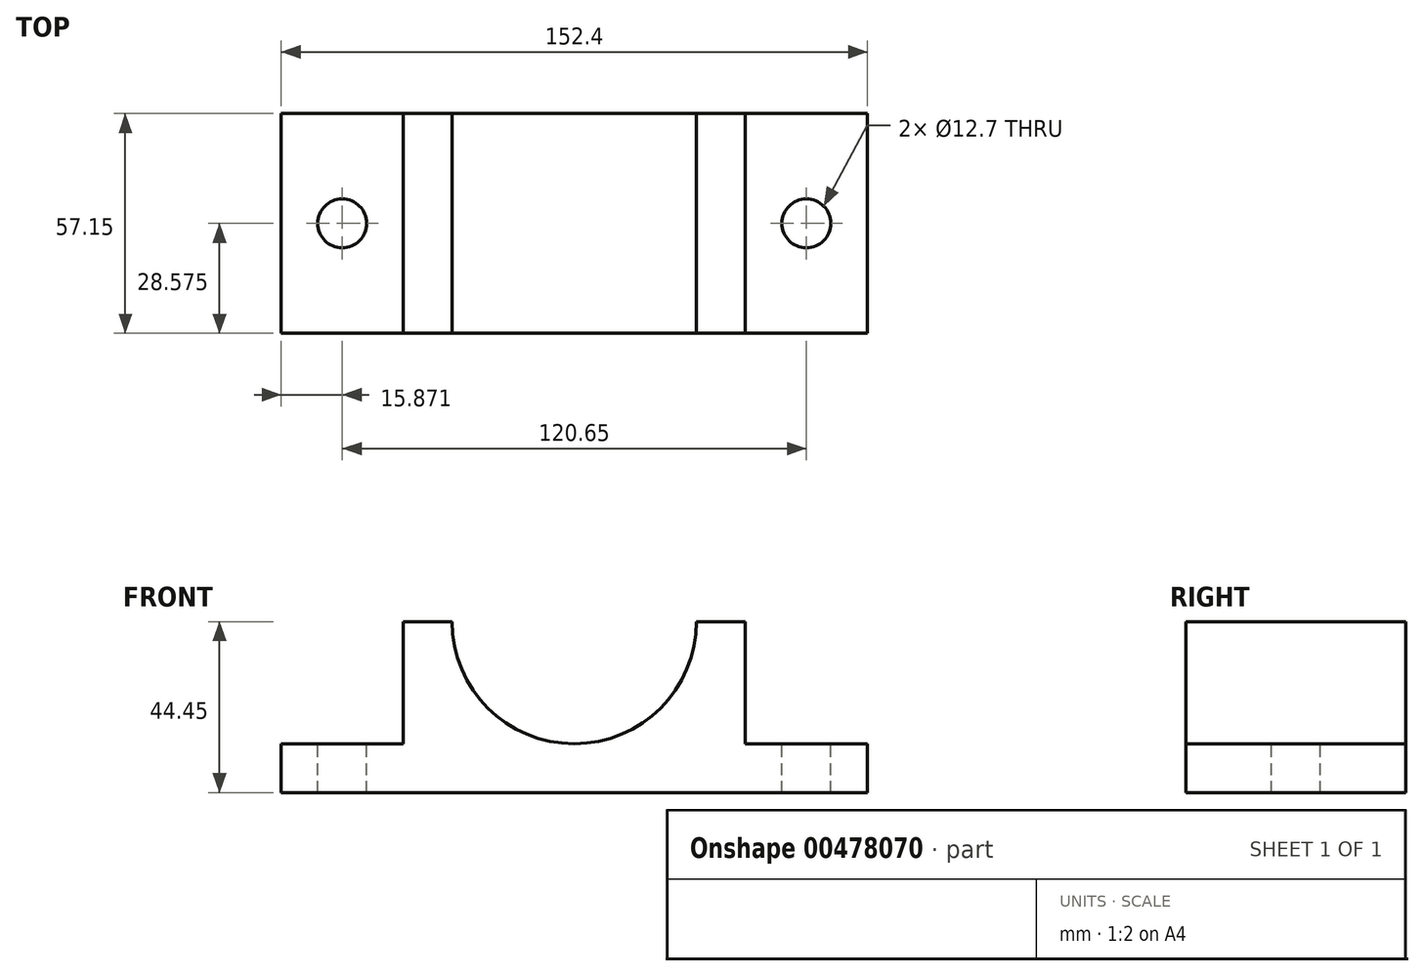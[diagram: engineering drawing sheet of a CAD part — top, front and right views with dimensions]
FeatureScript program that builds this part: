
annotation { "Feature Type Name" : "Feature", "Feature Type Description" : "" }
export const myFeature = defineFeature(function(context is Context, id is Id, definition is map)
    precondition{}
    {
        {
            var Q0;
            Q0=qCreatedBy(makeId("Front.planeOp"),FACE);
            var sketch = newSketch(context, id + "F0", { "sketchPlane" : qUnion([Q0])});
            skLineSegment(sketch, "E0", {"start": v(-44.61, 0) * mm, "end": v(107.79, 0) * mm});
            skLineSegment(sketch, "E1", {"start": v(107.79, 0) * mm, "end": v(107.79, 12.7) * mm});
            skLineSegment(sketch, "E2", {"start": v(107.79, 12.7) * mm, "end": v(76.04, 12.7) * mm});
            skLineSegment(sketch, "E3", {"start": v(76.04, 12.7) * mm, "end": v(76.04, 44.45) * mm});
            skLineSegment(sketch, "E4", {"start": v(76.04, 44.45) * mm, "end": v(63.34, 44.45) * mm});
            skLineSegment(sketch, "E5", {"start": v(-12.86, 44.45) * mm, "end": v(-12.86, 12.7) * mm});
            skLineSegment(sketch, "E6", {"start": v(-12.86, 12.7) * mm, "end": v(-44.61, 12.7) * mm});
            skLineSegment(sketch, "E7", {"start": v(-44.61, 12.7) * mm, "end": v(-44.61, 0) * mm});
            skArc(sketch, "E8", {"start": v(-0.16, 44.45) * mm, "mid": v(31.59, 12.7) * mm, "end": v(63.34, 44.45) * mm});
            skLineSegment(sketch, "E9.trimOffspring", {"start": v(-0.16, 44.45) * mm, "end": v(-12.86, 44.45) * mm});
            skSolve(sketch);
        }
        {
            var Q0;
            Q0=makeQuery(id+"F0.imprint","IMPRINT",FACE,{"disambiguationData":[TD([[makeQuery(id+"F0.imprint","IMPRINT",EDGE,{"derivedFrom":sQuery(id+"F0.wireOp",EDGE,"E0")}),1.0]])]});
            extrude(context, id + "F1", {"entities" : qUnion([Q0]), "depth" : 57.15 * mm});
        }
        {
            var Q0;
            Q0=makeQuery(id+"F1.opExtrude","SWEPT_FACE",FACE,{"disambiguationData":[OSD([sQuery(id+"F0.wireOp",EDGE,"E2")])]});
            var sketch = newSketch(context, id + "F2", { "sketchPlane" : qUnion([Q0])});
            skLineSegment(sketch, "E10", {"start": v(107.79, -57.15) * mm, "end": v(107.79, -28.58) * mm});
            skLineSegment(sketch, "E11", {"start": v(107.79, -28.58) * mm, "end": v(91.91, -28.58) * mm});
            skCircle(sketch, "E12", {"center": v(91.91, -28.58) * mm, "radius": 6.35 * mm});
            skSolve(sketch);
        }
        {
            var Q0;
            Q0 = qSketchRegion(id + "F2", true);
            extrude(context, id + "F3", {"entities" : qUnion([Q0]), "operationType" : NewBodyOperationType.REMOVE, "oppositeDirection" : true, "depth" : 25.4 * mm});
        }
        {
            var Q0;
            Q0=makeQuery(id+"F1.opExtrude","SWEPT_FACE",FACE,{"disambiguationData":[OSD([sQuery(id+"F0.wireOp",EDGE,"E6")])]});
            var sketch = newSketch(context, id + "F4", { "sketchPlane" : qUnion([Q0])});
            skLineSegment(sketch, "E13", {"start": v(-44.61, -57.15) * mm, "end": v(-44.61, -28.58) * mm});
            skLineSegment(sketch, "E14", {"start": v(-44.61, -28.58) * mm, "end": v(-28.74, -28.58) * mm});
            skCircle(sketch, "E15", {"center": v(-28.74, -28.58) * mm, "radius": 6.35 * mm});
            skSolve(sketch);
        }
        {
            var Q0;
            Q0 = qSketchRegion(id + "F4", true);
            extrude(context, id + "F5", {"entities" : qUnion([Q0]), "operationType" : NewBodyOperationType.REMOVE, "oppositeDirection" : true, "depth" : 25.4 * mm});
        }
    });
